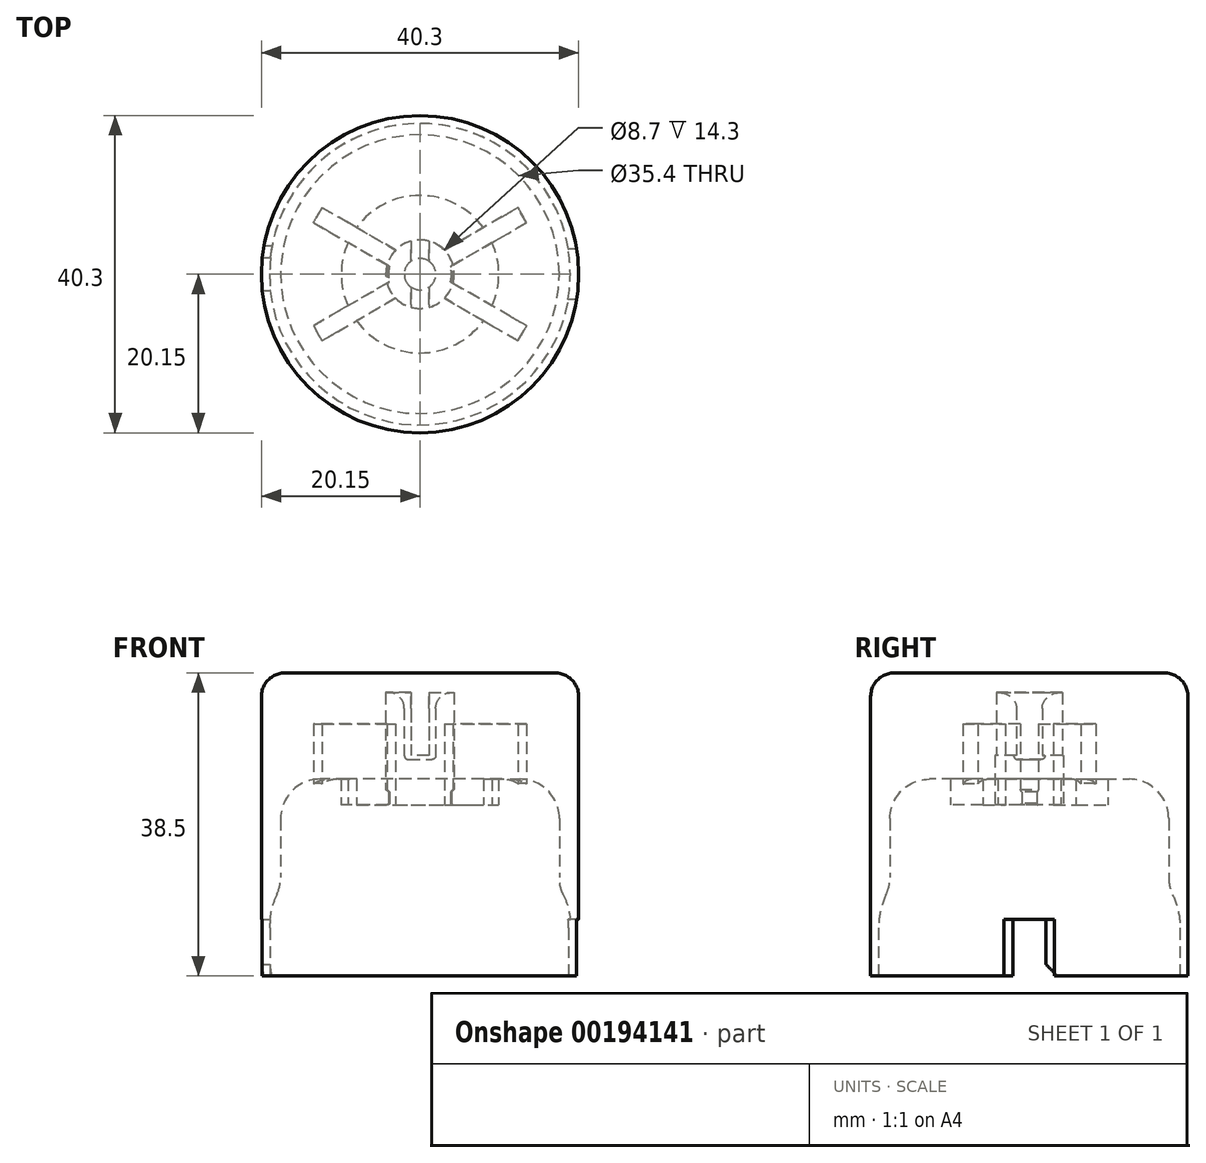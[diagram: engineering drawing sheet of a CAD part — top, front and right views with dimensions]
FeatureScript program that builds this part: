
annotation { "Feature Type Name" : "Feature", "Feature Type Description" : "" }
export const myFeature = defineFeature(function(context is Context, id is Id, definition is map)
    precondition{}
    {
        {
            var Q0;
            Q0=qCreatedBy(makeId("Front.planeOp"),FACE);
            var sketch = newSketch(context, id + "F0", { "sketchPlane" : qUnion([Q0])});
            skLineSegment(sketch, "E0", {"start": v(0, 38.5) * mm, "end": v(20.15, 38.5) * mm});
            skLineSegment(sketch, "E1", {"start": v(20.15, 38.5) * mm, "end": v(20.15, 0) * mm});
            skLineSegment(sketch, "E2", {"start": v(20.15, 0) * mm, "end": v(19.15, 0) * mm});
            skLineSegment(sketch, "E3", {"start": v(19.15, 0) * mm, "end": v(19.15, 9) * mm});
            skLineSegment(sketch, "E4", {"start": v(17.7, 9) * mm, "end": v(17.7, 25) * mm});
            skLineSegment(sketch, "E5", {"start": v(10, 21.7) * mm, "end": v(4.2, 21.7) * mm});
            skLineSegment(sketch, "E6", {"start": v(0, 27.5) * mm, "end": v(0, 38.5) * mm});
            skLineSegment(sketch, "E7", {"start": v(19.15, 9) * mm, "end": v(17.7, 9) * mm});
            skLineSegment(sketch, "E8", {"start": v(4, 23.35) * mm, "end": v(4, 21.9) * mm});
            skLineSegment(sketch, "E9", {"start": v(4, 23.35) * mm, "end": v(4, 23.35) * mm});
            skLineSegment(sketch, "E10", {"start": v(0, 27.5) * mm, "end": v(2, 27.5) * mm});
            skLineSegment(sketch, "E11", {"start": v(4.35, 36) * mm, "end": v(4.35, 23.7) * mm});
            skLineSegment(sketch, "E12", {"start": v(4.35, 23.7) * mm, "end": v(4, 23.35) * mm});
            skLineSegment(sketch, "E13", {"start": v(0, 0) * mm, "end": v(0, 86.8) * mm, "construction": true});
            skLineSegment(sketch, "E14", {"start": v(2, 27.5) * mm, "end": v(2, 36) * mm});
            skLineSegment(sketch, "E15", {"start": v(2, 36) * mm, "end": v(4.35, 36) * mm});
            skLineSegment(sketch, "E16", {"start": v(4, 21.9) * mm, "end": v(4.2, 21.7) * mm});
            skLineSegment(sketch, "E17", {"start": v(10, 21.7) * mm, "end": v(10, 25) * mm});
            skLineSegment(sketch, "E18", {"start": v(10, 25) * mm, "end": v(17.7, 25) * mm});
            skSolve(sketch);
        }
        {
            var Q0;
            Q0=makeQuery(id+"F0.imprint","IMPRINT",FACE,{"disambiguationData":[TD([[makeQuery(id+"F0.imprint","IMPRINT",EDGE,{"derivedFrom":sQuery(id+"F0.wireOp",EDGE,"E0")}),-1.0]])]});
            var Q1;
            Q1=sQuery(id+"F0.wireOp",EDGE,"YSzkctUK-GwUk-gnwC-o79f-ADjedX5dHt10");
            var Q2;
            Q2=sQuery(id+"F0.wireOp",EDGE,"E0");
            var Q3;
            Q3=sQuery(id+"F0.wireOp",EDGE,"E5");
            var Q4;
            Q4=sQuery(id+"F0.wireOp",EDGE,"E4");
            var Q5;
            Q5=sQuery(id+"F0.wireOp",EDGE,"XxiDbHku-afRg-uP6S-bizr-nLg15Vr7fEWh");
            var Q6;
            Q6=sQuery(id+"F0.wireOp",EDGE,"XZgHz5KV-8PCy-svoo-bFte-NMtHDqGm9mnZ");
            var Q7;
            Q7=sQuery(id+"F0.wireOp",EDGE,"E3");
            var Q8;
            Q8=sQuery(id+"F0.wireOp",EDGE,"E1");
            var Q9;
            Q9=sQuery(id+"F0.wireOp",EDGE,"E2");
            var Q10;
            Q10=sQuery(id+"F0.wireOp",EDGE,"E6");
            revolve(context, id + "F1", {"entities" : qUnion([Q0]), "surfaceEntities" : qUnion([Q1, Q2, Q3, Q4, Q5, Q6, Q7, Q8, Q9]), "axis" : qUnion([Q10]), "revolveType" : RevolveType.FULL});
        }
        {
            var Q0;
            Q0=makeQuery(id+"F1.opRevolve","SWEPT_EDGE",EDGE,{"disambiguationData":[OSD([sQuery(id+"F0.wireOp",EDGE,"E0"),sQuery(id+"F0.wireOp",EDGE,"E1")])]});
            fillet(context, id + "F2", {"entities" : qUnion([Q0]), "radius" : 3 * mm, "tangentPropagation" : true, "allowEdgeOverflow" : false});
        }
        {
            var Q0;
            Q0=qCreatedBy(makeId("Right.planeOp"),FACE);
            var sketch = newSketch(context, id + "F3", { "sketchPlane" : qUnion([Q0])});
            skLineSegment(sketch, "E19.bottom", {"start": v(-3.2, 7.2) * mm, "end": v(3.2, 7.2) * mm});
            skLineSegment(sketch, "E19.left", {"start": v(-3.2, 7.2) * mm, "end": v(-3.2, 0) * mm});
            skLineSegment(sketch, "E19.right", {"start": v(3.2, 7.2) * mm, "end": v(3.2, 0) * mm});
            skPoint(sketch, "E19.middle", {"position": v(0, 0) * mm});
            skLineSegment(sketch, "E20", {"start": v(-3.2, 0) * mm, "end": v(3.2, 0) * mm});
            skSolve(sketch);
        }
        {
            var Q0;
            Q0 = qSketchRegion(id + "F3", true);
            var Q1;
            Q1=makeQuery(id+"F1.opRevolve","SWEPT_FACE",FACE,{"disambiguationData":[OSD([sQuery(id+"F0.wireOp",EDGE,"E1")])]});
            extrude(context, id + "F4", {"entities" : qUnion([Q0]), "operationType" : NewBodyOperationType.REMOVE, "endBound" : BoundingType.UP_TO_SURFACE, "endBoundEntityFace" : qUnion([Q1]), "depth" : 100 * mm});
        }
        {
            var Q0;
            Q0=qCreatedBy(makeId("Right.planeOp"),FACE);
            var sketch = newSketch(context, id + "F5", { "sketchPlane" : qUnion([Q0])});
            skLineSegment(sketch, "E21.top", {"start": v(2.1, 7.2) * mm, "end": v(-2.1, 7.2) * mm});
            skLineSegment(sketch, "E21.left", {"start": v(2.1, 0) * mm, "end": v(2.1, 7.2) * mm});
            skLineSegment(sketch, "E21.right", {"start": v(-2.1, 0) * mm, "end": v(-2.1, 7.2) * mm});
            skPoint(sketch, "E21.middle", {"position": v(0, 0) * mm});
            skLineSegment(sketch, "E22", {"start": v(-2.1, 0) * mm, "end": v(2.1, 0) * mm});
            skSolve(sketch);
        }
        {
            var Q0;
            Q0 = qSketchRegion(id + "F5", true);
            extrude(context, id + "F6", {"entities" : qUnion([Q0]), "operationType" : NewBodyOperationType.REMOVE, "oppositeDirection" : true, "depth" : 25 * mm});
        }
        {
            var Q0;
            Q0=makeQuery(id+"F4.boolean.opBoolean","COPY",EDGE,{"disambiguationData":[OD(0.0)],"derivedFrom":makeQuery(id+"F4.opExtrude","SWEPT_EDGE",EDGE,{"disambiguationData":[OSD([sQuery(id+"F3.wireOp",EDGE,"E19.right"),sQuery(id+"F3.wireOp",EDGE,"E20")])]})});
            var Q1;
            Q1=makeQuery(id+"F4.boolean.opBoolean","COPY",EDGE,{"disambiguationData":[OD(0.0)],"derivedFrom":makeQuery(id+"F4.opExtrude","SWEPT_EDGE",EDGE,{"disambiguationData":[OSD([sQuery(id+"F3.wireOp",EDGE,"E19.left"),sQuery(id+"F3.wireOp",EDGE,"E20")])]})});
            var Q2;
            Q2=makeQuery(id+"F4.boolean.opBoolean","COPY",EDGE,{"disambiguationData":[OD(1.0)],"derivedFrom":makeQuery(id+"F4.opExtrude","SWEPT_EDGE",EDGE,{"disambiguationData":[OSD([sQuery(id+"F3.wireOp",EDGE,"E19.left"),sQuery(id+"F3.wireOp",EDGE,"E20")])]})});
            var Q3;
            Q3=makeQuery(id+"F4.boolean.opBoolean","COPY",EDGE,{"disambiguationData":[OD(1.0)],"derivedFrom":makeQuery(id+"F4.opExtrude","SWEPT_EDGE",EDGE,{"disambiguationData":[OSD([sQuery(id+"F3.wireOp",EDGE,"E19.right"),sQuery(id+"F3.wireOp",EDGE,"E20")])]})});
            var Q4;
            Q4=makeQuery(id+"F6.boolean.opBoolean","COPY",EDGE,{"derivedFrom":makeQuery(id+"F6.opExtrude","SWEPT_EDGE",EDGE,{"disambiguationData":[OSD([sQuery(id+"F5.wireOp",EDGE,"E21.right"),sQuery(id+"F5.wireOp",EDGE,"E22")])]})});
            var Q5;
            Q5=makeQuery(id+"F6.boolean.opBoolean","COPY",EDGE,{"derivedFrom":makeQuery(id+"F6.opExtrude","SWEPT_EDGE",EDGE,{"disambiguationData":[OSD([sQuery(id+"F5.wireOp",EDGE,"E21.left"),sQuery(id+"F5.wireOp",EDGE,"E22")])]})});
            chamfer(context, id + "F7", {"entities" : qUnion([Q0, Q1, Q2, Q3, Q4, Q5]), "width" : 1.5 * mm, "tangentPropagation" : true});
        }
        {
            var Q0;
            Q0=qCreatedBy(makeId("Top.planeOp"),FACE);
            var sketch = newSketch(context, id + "F8", { "sketchPlane" : qUnion([Q0])});
            skLineSegment(sketch, "E23", {"start": v(-13.54, 6.55) * mm, "end": v(-2.2, 0) * mm});
            skLineSegment(sketch, "E24", {"start": v(12.44, -8.45) * mm, "end": v(13.54, -6.55) * mm});
            skLineSegment(sketch, "E25", {"start": v(13.54, -6.55) * mm, "end": v(2.2, 0) * mm});
            skLineSegment(sketch, "E26", {"start": v(-12.44, 8.45) * mm, "end": v(-13.54, 6.55) * mm});
            skLineSegment(sketch, "E27", {"start": v(-23.05, 13.3) * mm, "end": v(-1.73, 1) * mm, "construction": true});
            skLineSegment(sketch, "E28", {"start": v(-12.44, -8.45) * mm, "end": v(-3.1, -3.06) * mm});
            skLineSegment(sketch, "E29", {"start": v(13.54, 6.55) * mm, "end": v(12.44, 8.45) * mm});
            skLineSegment(sketch, "E30", {"start": v(12.44, 8.45) * mm, "end": v(3.1, 3.06) * mm});
            skLineSegment(sketch, "E31", {"start": v(-13.54, -6.55) * mm, "end": v(-12.44, -8.45) * mm});
            skLineSegment(sketch, "E32", {"start": v(-22.92, -13.23) * mm, "end": v(-1.73, -1) * mm, "construction": true});
            skLineSegment(sketch, "E33.trimOffspring", {"start": v(-2.2, 0) * mm, "end": v(-13.54, -6.55) * mm});
            skLineSegment(sketch, "E34.trimOffspring", {"start": v(2.2, 0) * mm, "end": v(13.54, 6.55) * mm});
            skLineSegment(sketch, "E35.trimOffspring", {"start": v(-3.1, 3.06) * mm, "end": v(-12.44, 8.45) * mm});
            skLineSegment(sketch, "E36.trimOffspring", {"start": v(3.1, -3.06) * mm, "end": v(12.44, -8.45) * mm});
            skArc(sketch, "E37.trimOffspring", {"start": v(-3.1, -3.06) * mm, "mid": v(0, -4.35) * mm, "end": v(3.1, -3.06) * mm});
            skArc(sketch, "E38.trimOffspring", {"start": v(3.1, 3.06) * mm, "mid": v(0, 4.35) * mm, "end": v(-3.1, 3.06) * mm});
            skCircle(sketch, "E39", {"center": v(0, 0) * mm, "radius": 2 * mm});
            skLineSegment(sketch, "E40.trimOffspring", {"start": v(1.73, -1) * mm, "end": v(23.52, -13.58) * mm, "construction": true});
            skLineSegment(sketch, "E41.trimOffspring", {"start": v(1.73, 1) * mm, "end": v(23.69, 13.68) * mm, "construction": true});
            skSolve(sketch);
        }
        {
            var Q0;
            Q0 = qSketchRegion(id + "F8", true);
            extrude(context, id + "F9", {"entities" : qUnion([Q0]), "operationType" : NewBodyOperationType.REMOVE, "depth" : 32 * mm});
        }
        {
            var Q0;
            Q0=makeQuery(id+"F1.opRevolve","SWEPT_EDGE",EDGE,{"disambiguationData":[OSD([sQuery(id+"F0.wireOp",EDGE,"E4"),sQuery(id+"F0.wireOp",EDGE,"XxiDbHku-afRg-uP6S-bizr-nLg15Vr7fEWh")])]});
            fillet(context, id + "F10", {"entities" : qUnion([Q0]), "radius" : 5 * mm, "tangentPropagation" : true, "allowEdgeOverflow" : false});
        }
        {
            var Q0;
            Q0=makeQuery(id+"F1.opRevolve","SWEPT_EDGE",EDGE,{"disambiguationData":[OSD([sQuery(id+"F0.wireOp",EDGE,"E14"),sQuery(id+"F0.wireOp",EDGE,"E15")])]});
            fillet(context, id + "F11", {"entities" : qUnion([Q0]), "radius" : 2 * mm, "tangentPropagation" : true, "allowEdgeOverflow" : false});
        }
        {
            var Q0;
            Q0=makeQuery(id+"F1.opRevolve","SWEPT_FACE",FACE,{"disambiguationData":[OSD([sQuery(id+"F0.wireOp",EDGE,"E10")])]});
            fillet(context, id + "F12", {"entities" : qUnion([Q0]), "radius" : .5 * mm, "tangentPropagation" : true, "allowEdgeOverflow" : false});
        }
        {
            var Q0;
            Q0=makeQuery(id+"F10.opFillet","BLEND_EDGE",EDGE,{"blendedFrom":[makeQuery(id+"F1.opRevolve","SWEPT_EDGE",EDGE,{"disambiguationData":[OSD([sQuery(id+"F0.wireOp",EDGE,"E4"),sQuery(id+"F0.wireOp",EDGE,"E7")])]}),makeQuery(id+"F1.opRevolve","SWEPT_FACE",FACE,{"disambiguationData":[OSD([sQuery(id+"F0.wireOp",EDGE,"E3")])]})],"blendedInto":[makeQuery(id+"F1.opRevolve","SWEPT_FACE",FACE,{"disambiguationData":[OSD([sQuery(id+"F0.wireOp",EDGE,"E3")])]})]});
            fillet(context, id + "F13", {"entities" : qUnion([Q0]), "radius" : 10 * mm, "tangentPropagation" : true, "allowEdgeOverflow" : false});
        }
        {
            var Q0;
            Q0=qCreatedBy(makeId("Right.planeOp"),FACE);
            var sketch = newSketch(context, id + "F14", { "sketchPlane" : qUnion([Q0])});
            skLineSegment(sketch, "E42.bottom", {"start": v(9, 28) * mm, "end": v(-9, 28) * mm});
            skLineSegment(sketch, "E42.top", {"start": v(9, 36) * mm, "end": v(-9, 36) * mm});
            skLineSegment(sketch, "E42.left", {"start": v(9, 28) * mm, "end": v(9, 36) * mm});
            skLineSegment(sketch, "E42.right", {"start": v(-9, 28) * mm, "end": v(-9, 36) * mm});
            skPoint(sketch, "E42.middle", {"position": v(0, 32) * mm});
            skSolve(sketch);
        }
        {
            var Q0;
            Q0 = qSketchRegion(id + "F14", true);
            extrude(context, id + "F15", {"entities" : qUnion([Q0]), "operationType" : NewBodyOperationType.ADD, "endBound" : BoundingType.SYMMETRIC, "depth" : 2.3 * mm});
        }
    });
